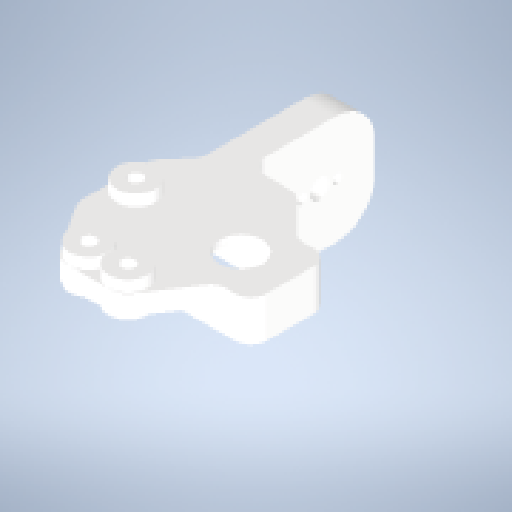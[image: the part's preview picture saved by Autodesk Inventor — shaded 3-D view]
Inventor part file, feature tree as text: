
AUTODESK INVENTOR PART (.ipt)
format: ipt  version: 2024 (Build 280153000, 153)  size: 264,704 bytes
history: native  units: in
note: dims shown in document units (in); Inventor stores cm internally (conversion verified against a paired STEP export)
features: extrude x3, sketch x3, plane x1, projected_geometry x1
ambient origin geometry x8: Origin, YZ Plane, XZ Plane, XY Plane, X Axis, Y Axis, Z Axis, Center Point
bodies: Solid2 (feature_tree), Solid1 (feature_tree)
feature tree (8):
  extrude  "Extrusion1"  Depth=0.1575in TaperAngle=0.0deg
  sketch  "Sketch3"  dims[d3=0.1575in d4=0.0in d5=0.0394in d6=0.0in]
  plane  "Work Plane1"
  extrude  "Extrusion2"  Depth=0.0394in TaperAngle=0.0deg
  extrude  "Extrusion3"  [1 undecoded]
  sketch  "Sketch1"  dims[d0=0.2953in d1=0.1575in d2=0.0in]
  projected_geometry  "Projected Loop2"
  sketch  "Sketch4"
note: 1 required parameter value undecoded (feature->parameter linkage not recoverable at this tier; creation-order binding heuristic only, values carry confidence <= 0.55)
